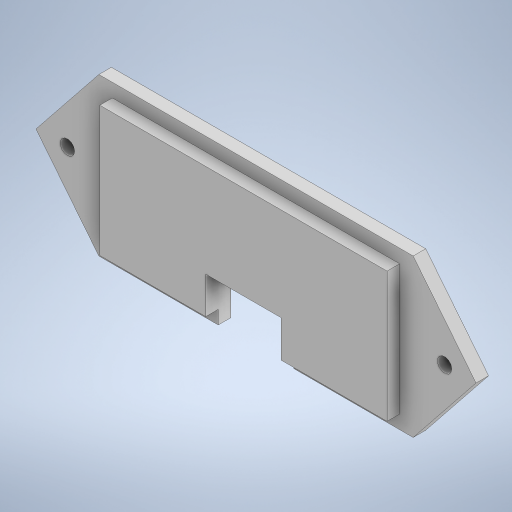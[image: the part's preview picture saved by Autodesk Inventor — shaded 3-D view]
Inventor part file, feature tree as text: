
AUTODESK INVENTOR PART (.ipt)
format: ipt  version: 2024 (Build 280153000, 153)  size: 247,808 bytes
history: native  units: mm
features: extrude x3, sketch x3
ambient origin geometry x8: Origin, YZ Plane, XZ Plane, XY Plane, X Axis, Y Axis, Z Axis, Center Point
bodies: Solid1 (feature_tree)
feature tree (6):
  extrude  "Extrusion1"  Depth=25.0mm
  extrude  "Extrusion4"  Depth=2.0mm
  extrude  "Extrusion5"  Depth=10.0mm
  sketch  "Sketch1"  dims[d0=50.0mm d1=25.0mm]
  sketch  "Sketch4"  dims[d2=2.0mm d3=0.0mm d18=12.5mm]
  sketch  "Sketch5"  dims[d19=10.0mm d20=10.0mm d21=2.3mm d22=2.3mm d23=5.0mm d24=5.0mm d25=20.7mm d26=2.15mm d27=45.7mm d28=2.15mm d29=2.0mm d30=0.0mm d31=19.0mm d32=12.0mm d33=8.0mm d34=0.0mm d35=0.0mm]
